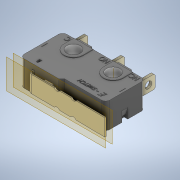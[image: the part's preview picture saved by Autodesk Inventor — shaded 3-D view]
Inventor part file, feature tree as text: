
AUTODESK INVENTOR PART (.ipt)
format: ipt  version: 2020 (Build 240168000, 168)  size: 1,313,792 bytes
history: native  units: mm
features: plane x4, projected_geometry x2, hole x1, other x1, sketch x1, imported_body x1
ambient origin geometry x8: Origin, YZ Plane, XZ Plane, XY Plane, X Axis, Y Axis, Z Axis, Center Point
bodies: Solid1 (feature_tree)
feature tree (10):
  plane  "Work Plane2"
  hole  "Hole1"  [1 undecoded]
  plane  "Work Plane3"
  plane  "Work Plane4"
  other  "Work Axis1"
  plane  "Work Plane1"
  sketch  "Sketch1"  dims[d0=0.0mm d1=9.1mm d2=-0.8mm d3=0.8mm d4=3.2004mm d5=5.9944mm d6=9.525mm d7=6.35mm d8=14.3117mm d9=8.7884mm d10=20.594885mm]
  projected_geometry  "Projected Loop1"
  projected_geometry  "Projected Loop2"
  imported_body  "Base1"
note: 1 required parameter value undecoded (feature->parameter linkage not recoverable at this tier; creation-order binding heuristic only, values carry confidence <= 0.55)
